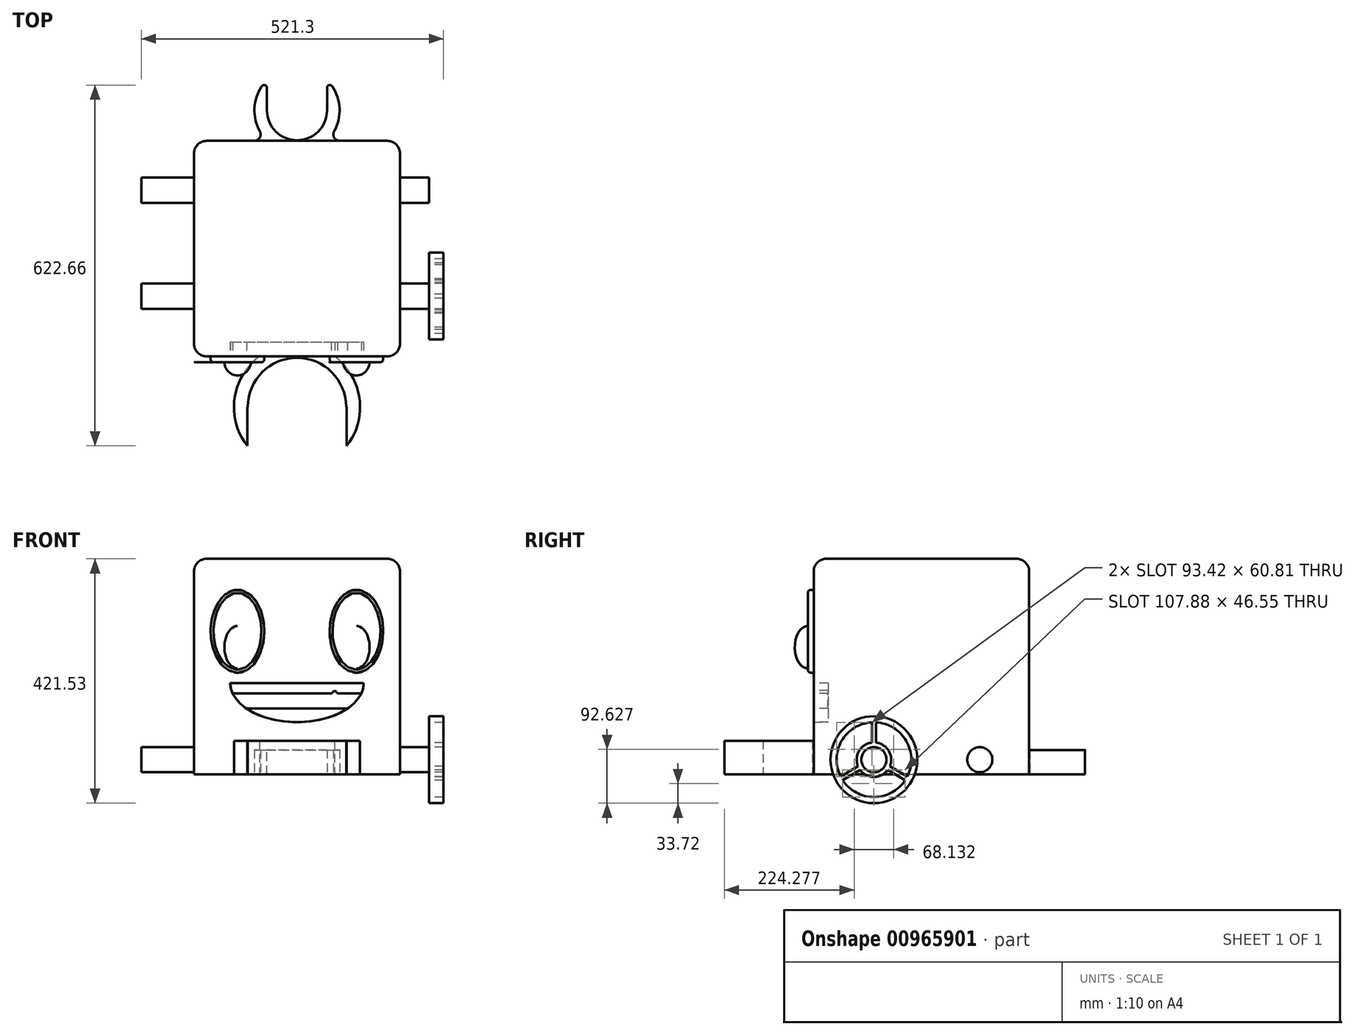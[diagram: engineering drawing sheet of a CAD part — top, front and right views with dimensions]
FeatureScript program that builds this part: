
annotation { "Feature Type Name" : "Feature", "Feature Type Description" : "" }
export const myFeature = defineFeature(function(context is Context, id is Id, definition is map)
    precondition{}
    {
        {
            var Q0;
            Q0=qCreatedBy(makeId("Front.planeOp"),FACE);
            var sketch = newSketch(context, id + "F0", { "sketchPlane" : qUnion([Q0])});
            skLineSegment(sketch, "E0.bottom", {"start": v(177.8, -185.93) * mm, "end": v(-177.8, -185.93) * mm});
            skLineSegment(sketch, "E0.top", {"start": v(177.8, 185.93) * mm, "end": v(-177.8, 185.93) * mm});
            skLineSegment(sketch, "E0.left", {"start": v(177.8, -185.93) * mm, "end": v(177.8, 185.93) * mm});
            skLineSegment(sketch, "E0.right", {"start": v(-177.8, -185.93) * mm, "end": v(-177.8, 185.93) * mm});
            skPoint(sketch, "E0.middle", {"position": v(0, 0) * mm});
            skSolve(sketch);
        }
        {
            var Q0;
            Q0=makeQuery(id+"F0.imprint","IMPRINT",FACE,{"disambiguationData":[TD([[makeQuery(id+"F0.imprint","IMPRINT",EDGE,{"derivedFrom":sQuery(id+"F0.wireOp",EDGE,"E0.bottom")}),-1.0]])]});
            extrude(context, id + "F1", {"entities" : qUnion([Q0]), "depth" : 371.86 * mm, "offsetDistance" : 25 * mm});
        }
        {
            var Q0;
            Q0=makeQuery(id+"F1.opExtrude","CAP_FACE",FACE,{"disambiguationData":[OSD([sQuery(id+"F0.wireOp",EDGE,"E0.bottom"),sQuery(id+"F0.wireOp",EDGE,"E0.top"),sQuery(id+"F0.wireOp",EDGE,"E0.left"),sQuery(id+"F0.wireOp",EDGE,"E0.right")])],"isStart":false});
            var sketch = newSketch(context, id + "F2", { "sketchPlane" : qUnion([Q0])});
            skEllipse(sketch, "E1", {"center": v(-102.64, 60.96) * mm, "majorRadius": 71.5 * mm, "minorRadius": 46.33 * mm, "majorAxis": v(0, -1)});
            skEllipse(sketch, "E2.MirrorC", {"center": v(102.64, 60.96) * mm, "majorRadius": 71.5 * mm, "minorRadius": 46.33 * mm, "majorAxis": v(0, -1)});
            skSolve(sketch);
        }
        {
            var Q0;
            Q0=makeQuery(id+"F2.imprint","IMPRINT",FACE,{"disambiguationData":[TD([[makeQuery(id+"F2.imprint","IMPRINT",EDGE,{"derivedFrom":sQuery(id+"F2.wireOp",EDGE,"E1")}),1.0]])]});
            var Q1;
            Q1=makeQuery(id+"F2.imprint","IMPRINT",FACE,{"disambiguationData":[TD([[makeQuery(id+"F2.imprint","IMPRINT",EDGE,{"derivedFrom":sQuery(id+"F2.wireOp",EDGE,"E2.MirrorC")}),1.0]])]});
            extrude(context, id + "F3", {"entities" : qUnion([Q0, Q1]), "depth" : 10 * mm, "offsetDistance" : 25 * mm});
        }
        {
            var Q0;
            Q0=makeQuery(id+"F3.opExtrude","CAP_FACE",FACE,{"disambiguationData":[OSD([sQuery(id+"F2.wireOp",EDGE,"E1")])],"isStart":false});
            var sketch = newSketch(context, id + "F4", { "sketchPlane" : qUnion([Q0])});
            skEllipticalArc(sketch, "E3", {});
            skEllipticalArc(sketch, "E4.MirrorC", {});
            skLineSegment(sketch, "E5", {"start": v(-102.64, 69.96) * mm, "end": v(-102.64, -3.15) * mm});
            skLineSegment(sketch, "E6", {"start": v(102.64, 69.96) * mm, "end": v(102.64, -3.15) * mm});
            const initialGuessF4  = {"E3": [-0.10264042764902115, 0.033403050154447556, 0, -1, 0.03655428811907768, 0.02275556683181465, 3.141592653589793, 0], "E4.MirrorC": [0.10264042764902115, 0.033403050154447556, 0, -1, 0.03655428811907768, 0.02275556683181465, 0, 3.141592653589793]};
            skSetInitialGuess(sketch, initialGuessF4);
            skSolve(sketch);
        }
        {
            var Q0;
            Q0=makeQuery(id+"F4.imprint","IMPRINT",FACE,{"disambiguationData":[TD([[makeQuery(id+"F4.imprint","IMPRINT",EDGE,{"derivedFrom":sQuery(id+"F4.wireOp",EDGE,"E3")}),1.0]])]});
            var Q1;
            Q1=sQuery(id+"F4.wireOp",EDGE,"E5");
            revolve(context, id + "F5", {"surfaceOperationType" : NewSurfaceOperationType.NEW, "entities" : qUnion([Q0]), "axis" : qUnion([Q1]), "revolveType" : RevolveType.ONE_DIRECTION, "oppositeDirection" : true, "angle" : 180 * degree});
        }
        {
            var Q0;
            Q0=makeQuery(id+"F4.imprint","IMPRINT",FACE,{"disambiguationData":[TD([[makeQuery(id+"F4.imprint","IMPRINT",EDGE,{"derivedFrom":sQuery(id+"F4.wireOp",EDGE,"E4.MirrorC")}),1.0]])]});
            var Q1;
            Q1=sQuery(id+"F4.wireOp",EDGE,"E6");
            revolve(context, id + "F6", {"surfaceOperationType" : NewSurfaceOperationType.NEW, "entities" : qUnion([Q0]), "axis" : qUnion([Q1]), "revolveType" : RevolveType.ONE_DIRECTION, "angle" : 180 * degree});
        }
        {
            var Q0;
            Q0=makeQuery(id+"F1.opExtrude","CAP_FACE",FACE,{"disambiguationData":[OSD([sQuery(id+"F0.wireOp",EDGE,"E0.bottom"),sQuery(id+"F0.wireOp",EDGE,"E0.top"),sQuery(id+"F0.wireOp",EDGE,"E0.left"),sQuery(id+"F0.wireOp",EDGE,"E0.right")])],"isStart":false});
            var sketch = newSketch(context, id + "F7", { "sketchPlane" : qUnion([Q0])});
            skEllipticalArc(sketch, "E7", {});
            skPoint(sketch, "E8.orphan", {"position": v(115.2, -66.43) * mm});
            skPoint(sketch, "E9.start.orphan", {"position": v(-115.2, -66.43) * mm});
            skLineSegment(sketch, "E10", {"start": v(-115.2, -28.43) * mm, "end": v(115.2, -28.43) * mm});
            skLineSegment(sketch, "E11", {"start": v(-110.95, -46.55) * mm, "end": v(59.45, -46.55) * mm});
            skLineSegment(sketch, "E12", {"start": v(59.45, -46.55) * mm, "end": v(65.24, -41.25) * mm});
            skLineSegment(sketch, "E13", {"start": v(65.24, -41.25) * mm, "end": v(70.08, -46.55) * mm});
            skLineSegment(sketch, "E14", {"start": v(70.08, -46.55) * mm, "end": v(110.95, -46.55) * mm});
            skLineSegment(sketch, "E15", {"start": v(-86.9, -72.63) * mm, "end": v(86.9, -72.63) * mm});
            const initialGuessF7  = {"E7": [0, -0.02842891216278076, 1, 0, 0.11520291864871979, 0.06732381357995788, 3.141592653589793, 0]};
            skSetInitialGuess(sketch, initialGuessF7);
            skSolve(sketch);
        }
        {
            var Q0;
            Q0=makeQuery(id+"F1.opExtrude","CAP_FACE",FACE,{"disambiguationData":[OSD([sQuery(id+"F0.wireOp",EDGE,"E0.bottom"),sQuery(id+"F0.wireOp",EDGE,"E0.top"),sQuery(id+"F0.wireOp",EDGE,"E0.left"),sQuery(id+"F0.wireOp",EDGE,"E0.right")])],"isStart":false});
            var sketch = newSketch(context, id + "F8", { "sketchPlane" : qUnion([Q0])});
            skEllipticalArc(sketch, "E16", {});
            skPoint(sketch, "E17.orphan", {"position": v(115.1, -66.38) * mm});
            skPoint(sketch, "E18.start.orphan", {"position": v(-115.3, -66.38) * mm});
            skLineSegment(sketch, "E19", {"start": v(-115.3, -28.38) * mm, "end": v(115.1, -28.38) * mm});
            skLineSegment(sketch, "E20", {"start": v(-111.06, -46.5) * mm, "end": v(59.34, -46.5) * mm});
            skLineSegment(sketch, "E21", {"start": v(59.34, -46.5) * mm, "end": v(65.14, -41.2) * mm});
            skLineSegment(sketch, "E22", {"start": v(65.14, -41.2) * mm, "end": v(69.98, -46.5) * mm});
            skLineSegment(sketch, "E23", {"start": v(69.98, -46.5) * mm, "end": v(110.85, -46.5) * mm});
            skLineSegment(sketch, "E24", {"start": v(-87, -72.59) * mm, "end": v(86.78, -72.59) * mm});
            skEllipticalArc(sketch, "E25.trimOffspring", {});
            skEllipticalArc(sketch, "E26.trimOffspring", {});
            const initialGuessF8  = {"E16": [-0.0001062229275703569, -0.028383396565914154, 1, 0, 0.11520291864871979, 0.06732381357995788, 3.141592653589793, 3.4140634112522834], "E25.trimOffspring": [-0.0001062229275703569, -0.028383396565914154, 1, 0, 0.11520291864871979, 0.06732381357995788, 3.8578909007786453, 5.566887059990733], "E26.trimOffspring": [-0.0001062229275703569, -0.028383396565914154, 1, 0, 0.11520291864871979, 0.06732381357995788, 6.010714549517095, 0]};
            skSetInitialGuess(sketch, initialGuessF8);
            skSolve(sketch);
        }
        {
            var Q0;
            {var subQ3=sQuery(id+"F7.wireOp",EDGE,"E11");Q0=makeQuery(id+"F7.imprint","IMPRINT",FACE,{"disambiguationData":[TD([[makeQuery(id+"F7.imprint","IMPRINT",EDGE,{"derivedFrom":subQ3}),-1.0]])]});}
            extrude(context, id + "F9", {"entities" : qUnion([Q0]), "operationType" : NewBodyOperationType.REMOVE, "oppositeDirection" : true, "depth" : 25 * mm, "offsetDistance" : 25 * mm});
        }
        {
            var Q0;
            Q0=makeQuery(id+"F9.boolean.opBoolean","COPY",FACE,{"derivedFrom":makeQuery(id+"F9.opExtrude","CAP_FACE",FACE,{"disambiguationData":[OSD([sQuery(id+"F7.wireOp",EDGE,"E7"),sQuery(id+"F7.wireOp",EDGE,"E11"),sQuery(id+"F7.wireOp",EDGE,"E12"),sQuery(id+"F7.wireOp",EDGE,"E13"),sQuery(id+"F7.wireOp",EDGE,"E14"),sQuery(id+"F7.wireOp",EDGE,"E15")])],"isStart":false})});
            extrude(context, id + "F10", {"entities" : qUnion([Q0]), "depth" : 0.5 * mm, "offsetDistance" : 25 * mm});
        }
        {
            var Q0;
            {var subQ1=sQuery(id+"F7.wireOp",EDGE,"E10");Q0=makeQuery(id+"F7.imprint","IMPRINT",FACE,{"disambiguationData":[TD([[makeQuery(id+"F7.imprint","IMPRINT",EDGE,{"derivedFrom":subQ1}),-1.0]])]});}
            var Q1;
            {var subQ0=sQuery(id+"F7.wireOp",EDGE,"E15");Q1=makeQuery(id+"F7.imprint","IMPRINT",FACE,{"disambiguationData":[TD([[makeQuery(id+"F7.imprint","IMPRINT",EDGE,{"derivedFrom":subQ0}),-1.0]])]});}
            extrude(context, id + "F11", {"entities" : qUnion([Q0, Q1]), "operationType" : NewBodyOperationType.REMOVE, "oppositeDirection" : true, "depth" : 25 * mm, "offsetDistance" : 25 * mm});
        }
        {
            var Q0;
            Q0=makeQuery(id+"F1.opExtrude","SWEPT_FACE",FACE,{"disambiguationData":[OSD([sQuery(id+"F0.wireOp",EDGE,"E0.bottom")])]});
            var sketch = newSketch(context, id + "F12", { "sketchPlane" : qUnion([Q0])});
            skArc(sketch, "E27", {"start": v(-84.86, 459.18) * mm, "mid": v(0, 374.31) * mm, "end": v(84.86, 459.18) * mm});
            skArc(sketch, "E28", {"start": v(-85.73, 526.27) * mm, "mid": v(0, 350.32) * mm, "end": v(85.72, 526.27) * mm});
            skLineSegment(sketch, "E29", {"start": v(-55.24, 494.6) * mm, "end": v(-55.24, 495.73) * mm});
            skLineSegment(sketch, "E30", {"start": v(55.24, 494.6) * mm, "end": v(55.24, 495.73) * mm});
            skPoint(sketch, "E31.start.orphan", {"position": v(-55.25, 430.18) * mm});
            skPoint(sketch, "E32.start.orphan", {"position": v(55.25, 430.18) * mm});
            skLineSegment(sketch, "E33.bottom", {"start": v(85.73, 430.18) * mm, "end": v(84.86, 430.18) * mm});
            skLineSegment(sketch, "E33.left", {"start": v(85.72, 459.18) * mm, "end": v(85.72, 526.27) * mm});
            skLineSegment(sketch, "E33.right", {"start": v(-85.73, 459.18) * mm, "end": v(-85.73, 526.27) * mm});
            skPoint(sketch, "E33.middle", {"position": v(0, 539.03) * mm});
            skLineSegment(sketch, "E34.trimOffspring", {"start": v(-84.86, 430.18) * mm, "end": v(-85.73, 430.18) * mm});
            skPoint(sketch, "E33.top.end.orphan", {"position": v(-85.73, 647.89) * mm});
            skPoint(sketch, "E33.top.start.orphan", {"position": v(85.73, 647.89) * mm});
            skLineSegment(sketch, "E35", {"start": v(85.72, 459.18) * mm, "end": v(84.86, 459.18) * mm});
            skLineSegment(sketch, "E36", {"start": v(-85.73, 459.18) * mm, "end": v(-84.86, 459.18) * mm});
            skSolve(sketch);
        }
        {
            var Q0;
            Q0=makeQuery(id+"F1.opExtrude","SWEPT_FACE",FACE,{"disambiguationData":[OSD([sQuery(id+"F0.wireOp",EDGE,"E0.left")])]});
            var sketch = newSketch(context, id + "F13", { "sketchPlane" : qUnion([Q0])});
            skCircle(sketch, "E37", {"center": v(-267.93, -160.66) * mm, "radius": 21.72 * mm});
            skCircle(sketch, "E38", {"center": v(-85.2, -160.66) * mm, "radius": 21.72 * mm});
            skSolve(sketch);
        }
        {
            var Q0;
            Q0=makeQuery(id+"F13.imprint","IMPRINT",FACE,{"disambiguationData":[TD([[makeQuery(id+"F13.imprint","IMPRINT",EDGE,{"derivedFrom":sQuery(id+"F13.wireOp",EDGE,"E37")}),1.0]])]});
            var Q1;
            Q1=makeQuery(id+"F13.imprint","IMPRINT",FACE,{"disambiguationData":[TD([[makeQuery(id+"F13.imprint","IMPRINT",EDGE,{"derivedFrom":sQuery(id+"F13.wireOp",EDGE,"E38")}),1.0]])]});
            extrude(context, id + "F14", {"entities" : qUnion([Q0, Q1]), "operationType" : NewBodyOperationType.ADD, "depth" : 50 * mm, "offsetDistance" : 25 * mm, "hasSecondDirection" : true, "secondDirectionOppositeDirection" : true, "secondDirectionDepth" : 446.3 * mm});
        }
        {
            var Q0;
            Q0=makeQuery(id+"F14.opExtrude","CAP_FACE",FACE,{"disambiguationData":[OSD([sQuery(id+"F13.wireOp",EDGE,"E37")])],"isStart":false});
            var sketch = newSketch(context, id + "F15", { "sketchPlane" : qUnion([Q0])});
            skCircle(sketch, "E39", {"center": v(-267.93, -160.66) * mm, "radius": 21.73 * mm});
            skCircle(sketch, "E40", {"center": v(-267.93, -160.66) * mm, "radius": 64.5 * mm});
            skArc(sketch, "E41", {"start": v(-271.59, -131.1) * mm, "mid": v(-293.72, -145.76) * mm, "end": v(-295.36, -172.27) * mm});
            skLineSegment(sketch, "E42.left", {"start": v(-264.27, -131.1) * mm, "end": v(-264.27, -96.26) * mm});
            skLineSegment(sketch, "E42.right", {"start": v(-271.59, -131.1) * mm, "end": v(-271.59, -96.26) * mm});
            skPoint(sketch, "E42.middle", {"position": v(-267.93, -113.51) * mm});
            skPoint(sketch, "E43.orphan", {"position": v(-267.93, -130.87) * mm});
            skPoint(sketch, "E44.end.orphan", {"position": v(-267.93, -96.16) * mm});
            skPoint(sketch, "E45.orphan", {"position": v(-264.27, -95.93) * mm});
            skPoint(sketch, "E46.orphan", {"position": v(-271.59, -95.93) * mm});
            skPoint(sketch, "E47.center", {"position": v(0, 0) * mm});
            skLineSegment(sketch, "E48.1.0", {"start": v(-291.7, -178.6) * mm, "end": v(-321.87, -196.02) * mm});
            skLineSegment(sketch, "E48.1.1", {"start": v(-295.36, -172.27) * mm, "end": v(-325.52, -189.68) * mm});
            skPoint(sketch, "E48.1.2", {"position": v(-541.02, -8.95) * mm});
            skLineSegment(sketch, "E48.2.0", {"start": v(-240.5, -172.27) * mm, "end": v(-210.33, -189.68) * mm});
            skLineSegment(sketch, "E48.2.1", {"start": v(-244.16, -178.6) * mm, "end": v(-213.99, -196.02) * mm});
            skPoint(sketch, "E48.2.2", {"position": v(-262.76, -473.02) * mm});
            skArc(sketch, "E49.trimOffspring", {"start": v(-291.7, -178.6) * mm, "mid": v(-267.93, -190.44) * mm, "end": v(-244.16, -178.6) * mm});
            skArc(sketch, "E50.trimOffspring", {"start": v(-240.5, -172.27) * mm, "mid": v(-242.13, -145.76) * mm, "end": v(-264.27, -131.1) * mm});
            skCircle(sketch, "E51", {"center": v(-267.93, -160.66) * mm, "radius": 74.94 * mm});
            skSolve(sketch);
        }
        {
            var Q0;
            Q0=makeQuery(id+"F15.imprint","IMPRINT",FACE,{"disambiguationData":[TD([[makeQuery(id+"F15.imprint","IMPRINT",EDGE,{"derivedFrom":sQuery(id+"F15.wireOp",EDGE,"E39")}),-1.0]])]});
            extrude(context, id + "F16", {"entities" : qUnion([Q0]), "depth" : 25 * mm, "offsetDistance" : 25 * mm});
        }
        {
            var Q0;
            Q0=makeQuery(id+"F15.imprint","IMPRINT",FACE,{"disambiguationData":[TD([[makeQuery(id+"F15.imprint","IMPRINT",EDGE,{"derivedFrom":sQuery(id+"F15.wireOp",EDGE,"E51")}),1.0]])]});
            extrude(context, id + "F17", {"entities" : qUnion([Q0]), "operationType" : NewBodyOperationType.ADD, "depth" : 25 * mm, "offsetDistance" : 25 * mm});
        }
        {
            var Q0;
            Q0=makeQuery(id+"F3.opExtrude","CAP_EDGE",EDGE,{"disambiguationData":[OSD([sQuery(id+"F2.wireOp",EDGE,"E1")])],"isStart":false});
            var Q1;
            Q1=makeQuery(id+"F3.opExtrude","CAP_EDGE",EDGE,{"disambiguationData":[OSD([sQuery(id+"F2.wireOp",EDGE,"E2.MirrorC")])],"isStart":false});
            var Q2;
            Q2=makeQuery(id+"F11.boolean.opBoolean","COPY",EDGE,{"derivedFrom":makeQuery(id+"F11.opExtrude","CAP_EDGE",EDGE,{"disambiguationData":[OSD([sQuery(id+"F7.wireOp",EDGE,"E10")])],"isStart":true})});
            fillet(context, id + "F18", {"entities" : qUnion([Q0, Q1, Q2]), "radius" : 5 * mm, "tangentPropagation" : true, "allowEdgeOverflow" : false});
        }
        {
            var Q0;
            Q0=makeQuery(id+"Fpzhqn44acI0Vzv_8.boolean.opBoolean","MERGE",FACE,{"derivedFrom":[makeQuery(id+"F1.opExtrude","SWEPT_FACE",FACE,{"disambiguationData":[OSD([sQuery(id+"F0.wireOp",EDGE,"E0.bottom")])]}),makeQuery(id+"Fpzhqn44acI0Vzv_8.opExtrude","CAP_FACE",FACE,{"disambiguationData":[OSD([sQuery(id+"F12.wireOp",EDGE,"E31"),sQuery(id+"F12.wireOp",EDGE,"E27"),sQuery(id+"F12.wireOp",EDGE,"u82ijdaK-Oqv1-Wm9l-6gOX-b4GgC8KagLjB"),sQuery(id+"F12.wireOp",EDGE,"E32")])],"isStart":true})]});
            var sketch = newSketch(context, id + "F19", { "sketchPlane" : qUnion([Q0])});
            skArc(sketch, "E52", {"start": v(51.82, -52.99) * mm, "mid": v(0, -1.17) * mm, "end": v(-51.82, -52.99) * mm});
            skArc(sketch, "E53", {"start": v(51.82, -105.22) * mm, "mid": v(0, 20.59) * mm, "end": v(-51.82, -105.22) * mm});
            skLineSegment(sketch, "E54.left", {"start": v(51.82, -52.99) * mm, "end": v(51.82, -105.22) * mm});
            skLineSegment(sketch, "E54.right", {"start": v(-51.82, -52.99) * mm, "end": v(-51.82, -105.22) * mm});
            skPoint(sketch, "E54.middle", {"position": v(0, -126.56) * mm});
            skSolve(sketch);
        }
        {
            var Q0;
            Q0=qSketchRegion(id+"F19",true);
            extrude(context, id + "F20", {"entities" : qUnion([Q0]), "operationType" : NewBodyOperationType.ADD, "oppositeDirection" : true, "depth" : 42 * mm, "offsetDistance" : 25 * mm});
        }
        {
            var Q0;
            Q0=makeQuery(id+"Fpzhqn44acI0Vzv_8.opExtrude","SWEPT_EDGE",EDGE,{"disambiguationData":[OSD([sQuery(id+"F12.wireOp",EDGE,"E27"),sQuery(id+"F12.wireOp",EDGE,"E32")])]});
            var Q1;
            Q1=makeQuery(id+"Fpzhqn44acI0Vzv_8.opExtrude","SWEPT_EDGE",EDGE,{"disambiguationData":[OSD([sQuery(id+"F12.wireOp",EDGE,"E27"),sQuery(id+"F12.wireOp",EDGE,"u82ijdaK-Oqv1-Wm9l-6gOX-b4GgC8KagLjB")])]});
            var Q2;
            Q2=makeQuery(id+"F20.opExtrude","SWEPT_EDGE",EDGE,{"disambiguationData":[OSD([sQuery(id+"F19.wireOp",EDGE,"E53"),sQuery(id+"F19.wireOp",EDGE,"E54.left")])]});
            var Q3;
            Q3=makeQuery(id+"F20.opExtrude","SWEPT_EDGE",EDGE,{"disambiguationData":[OSD([sQuery(id+"F19.wireOp",EDGE,"E53"),sQuery(id+"F19.wireOp",EDGE,"E54.right")])]});
            fillet(context, id + "F21", {"entities" : qUnion([Q0, Q1, Q2, Q3]), "radius" : 5 * mm, "tangentPropagation" : true, "allowEdgeOverflow" : false});
        }
        {
            var Q0;
            Q0=makeQuery(id+"F20.boolean.opBoolean","INTERSECT",EDGE,{"disambiguationData":[OD(0.0)],"derivedFrom":[makeQuery(id+"F1.opExtrude","CAP_FACE",FACE,{"disambiguationData":[OSD([sQuery(id+"F0.wireOp",EDGE,"E0.bottom"),sQuery(id+"F0.wireOp",EDGE,"E0.top"),sQuery(id+"F0.wireOp",EDGE,"E0.left"),sQuery(id+"F0.wireOp",EDGE,"E0.right")])],"isStart":true}),makeQuery(id+"F20.opExtrude","SWEPT_FACE",FACE,{"disambiguationData":[OSD([sQuery(id+"F19.wireOp",EDGE,"E53")])]})]});
            var Q1;
            Q1=makeQuery(id+"F20.boolean.opBoolean","INTERSECT",EDGE,{"disambiguationData":[OD(1.0)],"derivedFrom":[makeQuery(id+"F1.opExtrude","CAP_FACE",FACE,{"disambiguationData":[OSD([sQuery(id+"F0.wireOp",EDGE,"E0.bottom"),sQuery(id+"F0.wireOp",EDGE,"E0.top"),sQuery(id+"F0.wireOp",EDGE,"E0.left"),sQuery(id+"F0.wireOp",EDGE,"E0.right")])],"isStart":true}),makeQuery(id+"F20.opExtrude","SWEPT_FACE",FACE,{"disambiguationData":[OSD([sQuery(id+"F19.wireOp",EDGE,"E53")])]})]});
            fillet(context, id + "F22", {"entities" : qUnion([Q0, Q1]), "radius" : 11.35 * mm, "tangentPropagation" : true, "allowEdgeOverflow" : false});
        }
        {
            var Q0;
            Q0=makeQuery(id+"F1.opExtrude","CAP_EDGE",EDGE,{"disambiguationData":[OSD([sQuery(id+"F0.wireOp",EDGE,"E0.top")])],"isStart":false});
            var Q1;
            Q1=makeQuery(id+"F1.opExtrude","SWEPT_EDGE",EDGE,{"disambiguationData":[OSD([sQuery(id+"F0.wireOp",EDGE,"E0.top"),sQuery(id+"F0.wireOp",EDGE,"E0.left")])]});
            var Q2;
            Q2=makeQuery(id+"F1.opExtrude","CAP_EDGE",EDGE,{"disambiguationData":[OSD([sQuery(id+"F0.wireOp",EDGE,"E0.top")])],"isStart":true});
            var Q3;
            Q3=makeQuery(id+"F1.opExtrude","SWEPT_EDGE",EDGE,{"disambiguationData":[OSD([sQuery(id+"F0.wireOp",EDGE,"E0.top"),sQuery(id+"F0.wireOp",EDGE,"E0.right")])]});
            var Q4;
            Q4=makeQuery(id+"F1.opExtrude","CAP_EDGE",EDGE,{"disambiguationData":[OSD([sQuery(id+"F0.wireOp",EDGE,"E0.left")])],"isStart":false});
            var Q5;
            Q5=makeQuery(id+"F1.opExtrude","CAP_EDGE",EDGE,{"disambiguationData":[OSD([sQuery(id+"F0.wireOp",EDGE,"E0.left")])],"isStart":true});
            var Q6;
            Q6=makeQuery(id+"F1.opExtrude","CAP_EDGE",EDGE,{"disambiguationData":[OSD([sQuery(id+"F0.wireOp",EDGE,"E0.right")])],"isStart":false});
            var Q7;
            Q7=makeQuery(id+"F1.opExtrude","CAP_EDGE",EDGE,{"disambiguationData":[OSD([sQuery(id+"F0.wireOp",EDGE,"E0.right")])],"isStart":true});
            fillet(context, id + "F23", {"entities" : qUnion([Q0, Q1, Q2, Q3, Q4, Q5, Q6, Q7]), "radius" : 21.73 * mm, "tangentPropagation" : true, "allowEdgeOverflow" : false});
        }
        {
            var Q0;
            Q0=qSketchRegion(id+"F8",true);
            extrude(context, id + "F24", {"entities" : qUnion([Q0]), "oppositeDirection" : true, "depth" : 25 * mm, "offsetDistance" : 25 * mm});
        }
        {
            var Q0;
            Q0=makeQuery(id+"F12.imprint","IMPRINT",FACE,{"disambiguationData":[TD([[makeQuery(id+"F12.imprint","IMPRINT",EDGE,{"derivedFrom":sQuery(id+"F12.wireOp",EDGE,"E27")}),-1.0]])]});
            extrude(context, id + "F25", {"entities" : qUnion([Q0]), "operationType" : NewBodyOperationType.ADD, "oppositeDirection" : true, "depth" : 58 * mm, "offsetDistance" : 25 * mm});
        }
    });
